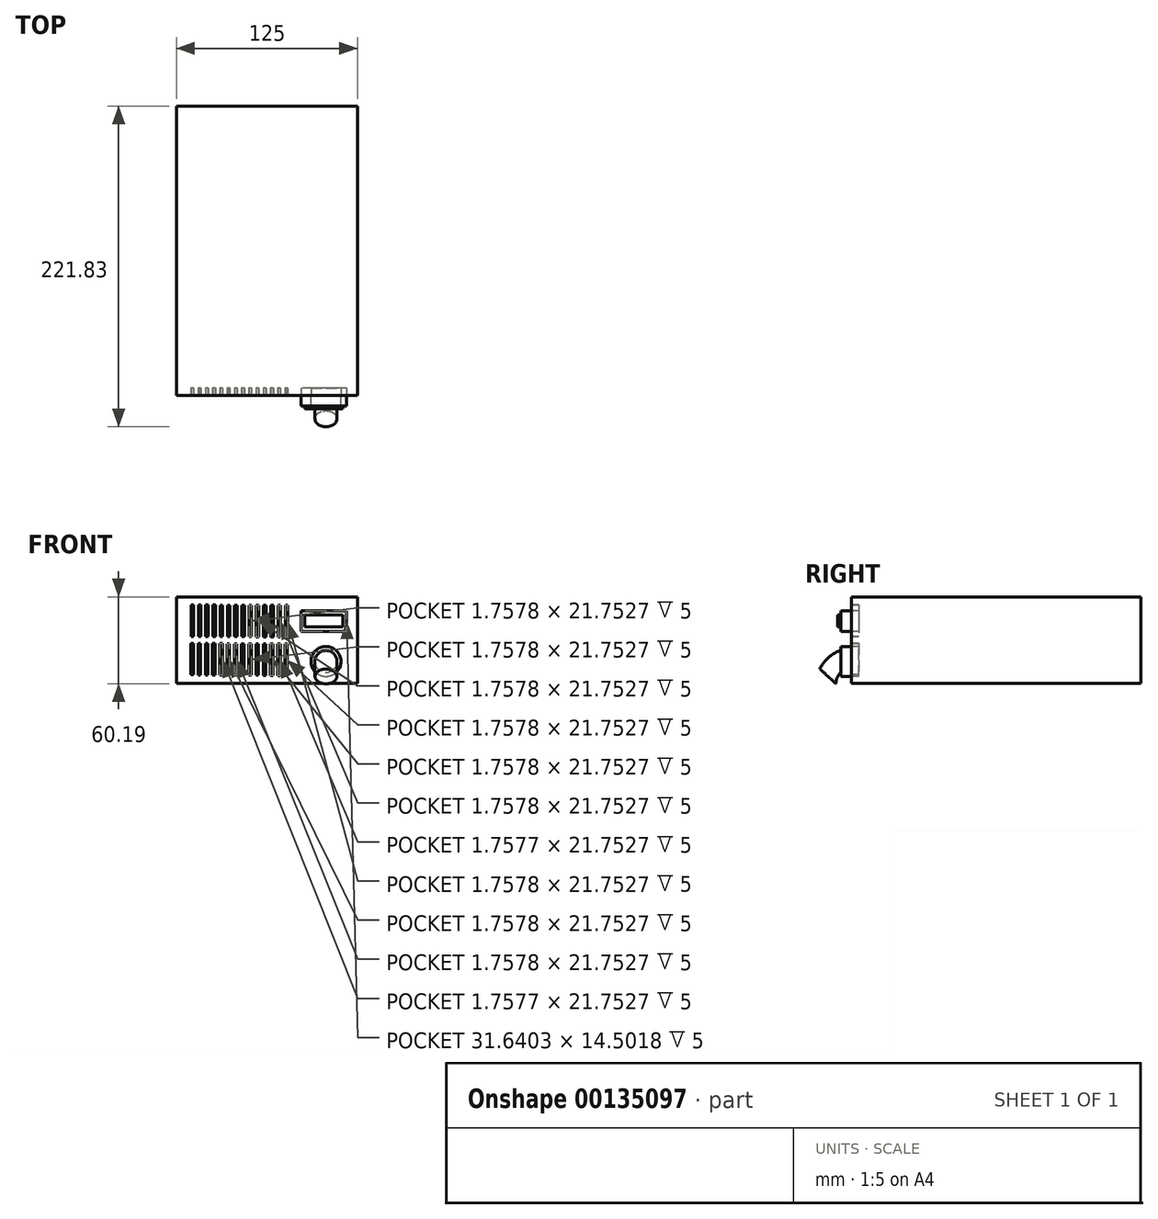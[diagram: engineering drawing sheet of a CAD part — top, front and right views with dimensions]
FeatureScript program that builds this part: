
annotation { "Feature Type Name" : "Feature", "Feature Type Description" : "" }
export const myFeature = defineFeature(function(context is Context, id is Id, definition is map)
    precondition{}
    {
        {
            var Q0;
            Q0=qCreatedBy(makeId("Front.planeOp"),FACE);
            var sketch = newSketch(context, id + "F0", { "sketchPlane" : qUnion([Q0])});
            skLineSegment(sketch, "E0.bottom", {"start": v(-38.13, -24.78) * mm, "end": v(86.87, -24.78) * mm});
            skLineSegment(sketch, "E0.top", {"start": v(-38.13, 35.22) * mm, "end": v(86.87, 35.22) * mm});
            skLineSegment(sketch, "E0.left", {"start": v(-38.13, -24.78) * mm, "end": v(-38.13, 35.22) * mm});
            skLineSegment(sketch, "E0.right", {"start": v(86.87, -24.78) * mm, "end": v(86.87, 35.22) * mm});
            skSolve(sketch);
        }
        {
            var Q0;
            Q0=makeQuery(id+"F0.imprint","IMPRINT",FACE,{"disambiguationData":[TD([[makeQuery(id+"F0.imprint","IMPRINT",EDGE,{"derivedFrom":sQuery(id+"F0.wireOp",EDGE,"E0.bottom")}),1.0]])]});
            extrude(context, id + "F1", {"entities" : qUnion([Q0]), "oppositeDirection" : true, "depth" : 200 * mm});
        }
        {
            var Q0;
            Q0=makeQuery(id+"F1.opExtrude","CAP_FACE",FACE,{"disambiguationData":[OSD([sQuery(id+"F0.wireOp",EDGE,"E0.bottom"),sQuery(id+"F0.wireOp",EDGE,"E0.top"),sQuery(id+"F0.wireOp",EDGE,"E0.left"),sQuery(id+"F0.wireOp",EDGE,"E0.right")])],"isStart":true});
            var sketch = newSketch(context, id + "F2", { "sketchPlane" : qUnion([Q0])});
            skLineSegment(sketch, "E1.bottom", {"start": v(79.42, 25.68) * mm, "end": v(47.78, 25.68) * mm});
            skLineSegment(sketch, "E1.top", {"start": v(79.42, 11.18) * mm, "end": v(47.78, 11.18) * mm});
            skLineSegment(sketch, "E1.left", {"start": v(79.42, 25.68) * mm, "end": v(79.42, 11.18) * mm});
            skLineSegment(sketch, "E1.right", {"start": v(47.78, 25.68) * mm, "end": v(47.78, 11.18) * mm});
            skCircle(sketch, "E2", {"center": v(65.14, -9.48) * mm, "radius": 10.36 * mm});
            skLineSegment(sketch, "E3.bottom", {"start": v(-26.27, 29.64) * mm, "end": v(-28.03, 29.64) * mm});
            skLineSegment(sketch, "E3.top", {"start": v(-26.27, 7.88) * mm, "end": v(-28.03, 7.88) * mm});
            skLineSegment(sketch, "E3.left", {"start": v(-26.27, 29.64) * mm, "end": v(-26.27, 7.88) * mm});
            skLineSegment(sketch, "E3.right", {"start": v(-28.03, 29.64) * mm, "end": v(-28.03, 7.88) * mm});
            skLineSegment(sketch, "E4.0.1.0", {"start": v(-28.25, 3) * mm, "end": v(-28.25, -18.75) * mm});
            skLineSegment(sketch, "E4.0.1.1", {"start": v(-26.49, 3) * mm, "end": v(-26.49, -18.75) * mm});
            skLineSegment(sketch, "E4.0.1.2", {"start": v(-26.49, 3) * mm, "end": v(-28.25, 3) * mm});
            skLineSegment(sketch, "E4.0.1.3", {"start": v(-26.49, -18.75) * mm, "end": v(-28.25, -18.75) * mm});
            skLineSegment(sketch, "E4.1.0.0", {"start": v(-23.03, 29.6) * mm, "end": v(-23.03, 7.85) * mm});
            skLineSegment(sketch, "E4.1.0.1", {"start": v(-21.27, 29.6) * mm, "end": v(-21.27, 7.85) * mm});
            skLineSegment(sketch, "E4.1.0.2", {"start": v(-21.27, 29.6) * mm, "end": v(-23.03, 29.6) * mm});
            skLineSegment(sketch, "E4.1.0.3", {"start": v(-21.27, 7.85) * mm, "end": v(-23.03, 7.85) * mm});
            skLineSegment(sketch, "E4.1.1.0", {"start": v(-23.25, 2.97) * mm, "end": v(-23.25, -18.79) * mm});
            skLineSegment(sketch, "E4.1.1.1", {"start": v(-21.49, 2.97) * mm, "end": v(-21.49, -18.79) * mm});
            skLineSegment(sketch, "E4.1.1.2", {"start": v(-21.49, 2.97) * mm, "end": v(-23.25, 2.97) * mm});
            skLineSegment(sketch, "E4.1.1.3", {"start": v(-21.49, -18.79) * mm, "end": v(-23.25, -18.79) * mm});
            skLineSegment(sketch, "E4.2.0.0", {"start": v(-18.03, 29.57) * mm, "end": v(-18.03, 7.82) * mm});
            skLineSegment(sketch, "E4.2.0.1", {"start": v(-16.27, 29.57) * mm, "end": v(-16.27, 7.82) * mm});
            skLineSegment(sketch, "E4.2.0.2", {"start": v(-16.27, 29.57) * mm, "end": v(-18.03, 29.57) * mm});
            skLineSegment(sketch, "E4.2.0.3", {"start": v(-16.27, 7.82) * mm, "end": v(-18.03, 7.82) * mm});
            skLineSegment(sketch, "E4.2.1.0", {"start": v(-18.25, 2.93) * mm, "end": v(-18.25, -18.82) * mm});
            skLineSegment(sketch, "E4.2.1.1", {"start": v(-16.49, 2.93) * mm, "end": v(-16.49, -18.82) * mm});
            skLineSegment(sketch, "E4.2.1.2", {"start": v(-16.49, 2.93) * mm, "end": v(-18.25, 2.93) * mm});
            skLineSegment(sketch, "E4.2.1.3", {"start": v(-16.49, -18.82) * mm, "end": v(-18.25, -18.82) * mm});
            skLineSegment(sketch, "E4.direction1", {"start": v(-28.03, 7.88) * mm, "end": v(-23.03, 7.85) * mm, "construction": true});
            skLineSegment(sketch, "E4.direction2", {"start": v(-28.03, 7.88) * mm, "end": v(-28.25, -18.75) * mm, "construction": true});
            skLineSegment(sketch, "E5.0.3.0", {"start": v(-13.03, 29.53) * mm, "end": v(-13.03, 7.78) * mm});
            skLineSegment(sketch, "E5.3.3.0", {"start": v(-11.27, 29.53) * mm, "end": v(-11.27, 7.78) * mm});
            skLineSegment(sketch, "E5.6.3.0", {"start": v(-11.27, 29.53) * mm, "end": v(-13.03, 29.53) * mm});
            skLineSegment(sketch, "E5.9.3.0", {"start": v(-11.27, 7.78) * mm, "end": v(-13.03, 7.78) * mm});
            skLineSegment(sketch, "E5.0.3.1", {"start": v(-13.25, 2.9) * mm, "end": v(-13.25, -18.85) * mm});
            skLineSegment(sketch, "E5.3.3.1", {"start": v(-11.49, 2.9) * mm, "end": v(-11.49, -18.85) * mm});
            skLineSegment(sketch, "E5.6.3.1", {"start": v(-11.49, 2.9) * mm, "end": v(-13.25, 2.9) * mm});
            skLineSegment(sketch, "E5.9.3.1", {"start": v(-11.49, -18.85) * mm, "end": v(-13.25, -18.85) * mm});
            skLineSegment(sketch, "E5.0.4.0", {"start": v(-8.03, 29.5) * mm, "end": v(-8.03, 7.75) * mm});
            skLineSegment(sketch, "E5.3.4.0", {"start": v(-6.27, 29.5) * mm, "end": v(-6.27, 7.75) * mm});
            skLineSegment(sketch, "E5.6.4.0", {"start": v(-6.27, 29.5) * mm, "end": v(-8.03, 29.5) * mm});
            skLineSegment(sketch, "E5.9.4.0", {"start": v(-6.27, 7.75) * mm, "end": v(-8.03, 7.75) * mm});
            skLineSegment(sketch, "E5.0.4.1", {"start": v(-8.25, 2.87) * mm, "end": v(-8.25, -18.89) * mm});
            skLineSegment(sketch, "E5.3.4.1", {"start": v(-6.49, 2.87) * mm, "end": v(-6.49, -18.89) * mm});
            skLineSegment(sketch, "E5.6.4.1", {"start": v(-6.49, 2.87) * mm, "end": v(-8.25, 2.87) * mm});
            skLineSegment(sketch, "E5.9.4.1", {"start": v(-6.49, -18.89) * mm, "end": v(-8.25, -18.89) * mm});
            skLineSegment(sketch, "E5.0.5.0", {"start": v(-3.03, 29.47) * mm, "end": v(-3.03, 7.72) * mm});
            skLineSegment(sketch, "E5.3.5.0", {"start": v(-1.27, 29.47) * mm, "end": v(-1.27, 7.72) * mm});
            skLineSegment(sketch, "E5.6.5.0", {"start": v(-1.27, 29.47) * mm, "end": v(-3.03, 29.47) * mm});
            skLineSegment(sketch, "E5.9.5.0", {"start": v(-1.27, 7.72) * mm, "end": v(-3.03, 7.72) * mm});
            skLineSegment(sketch, "E5.0.5.1", {"start": v(-3.25, 2.83) * mm, "end": v(-3.25, -18.92) * mm});
            skLineSegment(sketch, "E5.3.5.1", {"start": v(-1.49, 2.83) * mm, "end": v(-1.49, -18.92) * mm});
            skLineSegment(sketch, "E5.6.5.1", {"start": v(-1.49, 2.83) * mm, "end": v(-3.25, 2.83) * mm});
            skLineSegment(sketch, "E5.9.5.1", {"start": v(-1.49, -18.92) * mm, "end": v(-3.25, -18.92) * mm});
            skLineSegment(sketch, "E5.0.6.0", {"start": v(1.97, 29.43) * mm, "end": v(1.97, 7.68) * mm});
            skLineSegment(sketch, "E5.3.6.0", {"start": v(3.73, 29.43) * mm, "end": v(3.73, 7.68) * mm});
            skLineSegment(sketch, "E5.6.6.0", {"start": v(3.73, 29.43) * mm, "end": v(1.97, 29.43) * mm});
            skLineSegment(sketch, "E5.9.6.0", {"start": v(3.73, 7.68) * mm, "end": v(1.97, 7.68) * mm});
            skLineSegment(sketch, "E5.0.6.1", {"start": v(1.75, 2.8) * mm, "end": v(1.75, -18.95) * mm});
            skLineSegment(sketch, "E5.3.6.1", {"start": v(3.51, 2.8) * mm, "end": v(3.51, -18.95) * mm});
            skLineSegment(sketch, "E5.6.6.1", {"start": v(3.51, 2.8) * mm, "end": v(1.75, 2.8) * mm});
            skLineSegment(sketch, "E5.9.6.1", {"start": v(3.51, -18.95) * mm, "end": v(1.75, -18.95) * mm});
            skLineSegment(sketch, "E5.0.7.0", {"start": v(6.97, 29.4) * mm, "end": v(6.97, 7.65) * mm});
            skLineSegment(sketch, "E5.3.7.0", {"start": v(8.73, 29.4) * mm, "end": v(8.73, 7.65) * mm});
            skLineSegment(sketch, "E5.6.7.0", {"start": v(8.73, 29.4) * mm, "end": v(6.97, 29.4) * mm});
            skLineSegment(sketch, "E5.9.7.0", {"start": v(8.73, 7.65) * mm, "end": v(6.97, 7.65) * mm});
            skLineSegment(sketch, "E5.0.7.1", {"start": v(6.75, 2.77) * mm, "end": v(6.75, -18.99) * mm});
            skLineSegment(sketch, "E5.3.7.1", {"start": v(8.51, 2.77) * mm, "end": v(8.51, -18.99) * mm});
            skLineSegment(sketch, "E5.6.7.1", {"start": v(8.51, 2.77) * mm, "end": v(6.75, 2.77) * mm});
            skLineSegment(sketch, "E5.9.7.1", {"start": v(8.51, -18.99) * mm, "end": v(6.75, -18.99) * mm});
            skLineSegment(sketch, "E5.0.8.0", {"start": v(11.97, 29.37) * mm, "end": v(11.97, 7.61) * mm});
            skLineSegment(sketch, "E5.3.8.0", {"start": v(13.73, 29.37) * mm, "end": v(13.73, 7.61) * mm});
            skLineSegment(sketch, "E5.6.8.0", {"start": v(13.73, 29.37) * mm, "end": v(11.97, 29.37) * mm});
            skLineSegment(sketch, "E5.9.8.0", {"start": v(13.73, 7.61) * mm, "end": v(11.97, 7.61) * mm});
            skLineSegment(sketch, "E5.0.8.1", {"start": v(11.75, 2.73) * mm, "end": v(11.75, -19.02) * mm});
            skLineSegment(sketch, "E5.3.8.1", {"start": v(13.51, 2.73) * mm, "end": v(13.51, -19.02) * mm});
            skLineSegment(sketch, "E5.6.8.1", {"start": v(13.51, 2.73) * mm, "end": v(11.75, 2.73) * mm});
            skLineSegment(sketch, "E5.9.8.1", {"start": v(13.51, -19.02) * mm, "end": v(11.75, -19.02) * mm});
            skLineSegment(sketch, "E5.0.9.0", {"start": v(16.97, 29.33) * mm, "end": v(16.97, 7.58) * mm});
            skLineSegment(sketch, "E5.3.9.0", {"start": v(18.73, 29.33) * mm, "end": v(18.73, 7.58) * mm});
            skLineSegment(sketch, "E5.6.9.0", {"start": v(18.73, 29.33) * mm, "end": v(16.97, 29.33) * mm});
            skLineSegment(sketch, "E5.9.9.0", {"start": v(18.73, 7.58) * mm, "end": v(16.97, 7.58) * mm});
            skLineSegment(sketch, "E5.0.9.1", {"start": v(16.75, 2.7) * mm, "end": v(16.75, -19.05) * mm});
            skLineSegment(sketch, "E5.3.9.1", {"start": v(18.51, 2.7) * mm, "end": v(18.51, -19.05) * mm});
            skLineSegment(sketch, "E5.6.9.1", {"start": v(18.51, 2.7) * mm, "end": v(16.75, 2.7) * mm});
            skLineSegment(sketch, "E5.9.9.1", {"start": v(18.51, -19.05) * mm, "end": v(16.75, -19.05) * mm});
            skLineSegment(sketch, "E5.0.10.0", {"start": v(21.97, 29.3) * mm, "end": v(21.97, 7.55) * mm});
            skLineSegment(sketch, "E5.3.10.0", {"start": v(23.73, 29.3) * mm, "end": v(23.73, 7.55) * mm});
            skLineSegment(sketch, "E5.6.10.0", {"start": v(23.73, 29.3) * mm, "end": v(21.97, 29.3) * mm});
            skLineSegment(sketch, "E5.9.10.0", {"start": v(23.73, 7.55) * mm, "end": v(21.97, 7.55) * mm});
            skLineSegment(sketch, "E5.0.10.1", {"start": v(21.75, 2.66) * mm, "end": v(21.75, -19.09) * mm});
            skLineSegment(sketch, "E5.3.10.1", {"start": v(23.51, 2.66) * mm, "end": v(23.51, -19.09) * mm});
            skLineSegment(sketch, "E5.6.10.1", {"start": v(23.51, 2.66) * mm, "end": v(21.75, 2.66) * mm});
            skLineSegment(sketch, "E5.9.10.1", {"start": v(23.51, -19.09) * mm, "end": v(21.75, -19.09) * mm});
            skLineSegment(sketch, "E5.0.11.0", {"start": v(26.97, 29.27) * mm, "end": v(26.97, 7.51) * mm});
            skLineSegment(sketch, "E5.3.11.0", {"start": v(28.73, 29.27) * mm, "end": v(28.73, 7.51) * mm});
            skLineSegment(sketch, "E5.6.11.0", {"start": v(28.73, 29.27) * mm, "end": v(26.97, 29.27) * mm});
            skLineSegment(sketch, "E5.9.11.0", {"start": v(28.73, 7.51) * mm, "end": v(26.97, 7.51) * mm});
            skLineSegment(sketch, "E5.0.11.1", {"start": v(26.75, 2.63) * mm, "end": v(26.75, -19.12) * mm});
            skLineSegment(sketch, "E5.3.11.1", {"start": v(28.51, 2.63) * mm, "end": v(28.51, -19.12) * mm});
            skLineSegment(sketch, "E5.6.11.1", {"start": v(28.51, 2.63) * mm, "end": v(26.75, 2.63) * mm});
            skLineSegment(sketch, "E5.9.11.1", {"start": v(28.51, -19.12) * mm, "end": v(26.75, -19.12) * mm});
            skLineSegment(sketch, "E5.0.12.0", {"start": v(31.97, 29.23) * mm, "end": v(31.97, 7.48) * mm});
            skLineSegment(sketch, "E5.3.12.0", {"start": v(33.73, 29.23) * mm, "end": v(33.73, 7.48) * mm});
            skLineSegment(sketch, "E5.6.12.0", {"start": v(33.73, 29.23) * mm, "end": v(31.97, 29.23) * mm});
            skLineSegment(sketch, "E5.9.12.0", {"start": v(33.73, 7.48) * mm, "end": v(31.97, 7.48) * mm});
            skLineSegment(sketch, "E5.0.12.1", {"start": v(31.75, 2.6) * mm, "end": v(31.75, -19.16) * mm});
            skLineSegment(sketch, "E5.3.12.1", {"start": v(33.51, 2.6) * mm, "end": v(33.51, -19.16) * mm});
            skLineSegment(sketch, "E5.6.12.1", {"start": v(33.51, 2.6) * mm, "end": v(31.75, 2.6) * mm});
            skLineSegment(sketch, "E5.9.12.1", {"start": v(33.51, -19.16) * mm, "end": v(31.75, -19.16) * mm});
            skLineSegment(sketch, "E5.0.13.0", {"start": v(36.97, 29.2) * mm, "end": v(36.97, 7.45) * mm});
            skLineSegment(sketch, "E5.3.13.0", {"start": v(38.73, 29.2) * mm, "end": v(38.73, 7.45) * mm});
            skLineSegment(sketch, "E5.6.13.0", {"start": v(38.73, 29.2) * mm, "end": v(36.97, 29.2) * mm});
            skLineSegment(sketch, "E5.9.13.0", {"start": v(38.73, 7.45) * mm, "end": v(36.97, 7.45) * mm});
            skLineSegment(sketch, "E5.0.13.1", {"start": v(36.75, 2.56) * mm, "end": v(36.75, -19.19) * mm});
            skLineSegment(sketch, "E5.3.13.1", {"start": v(38.51, 2.56) * mm, "end": v(38.51, -19.19) * mm});
            skLineSegment(sketch, "E5.6.13.1", {"start": v(38.51, 2.56) * mm, "end": v(36.75, 2.56) * mm});
            skLineSegment(sketch, "E5.9.13.1", {"start": v(38.51, -19.19) * mm, "end": v(36.75, -19.19) * mm});
            skSolve(sketch);
        }
        {
            var Q0;
            Q0=makeQuery(id+"F2.imprint","IMPRINT",FACE,{"disambiguationData":[TD([[makeQuery(id+"F2.imprint","IMPRINT",EDGE,{"derivedFrom":sQuery(id+"F2.wireOp",EDGE,"E1.bottom")}),1.0]])]});
            var Q1;
            Q1=makeQuery(id+"F2.imprint","IMPRINT",FACE,{"disambiguationData":[TD([[makeQuery(id+"F2.imprint","IMPRINT",EDGE,{"derivedFrom":sQuery(id+"F2.wireOp",EDGE,"E2")}),1.0]])]});
            extrude(context, id + "F3", {"entities" : qUnion([Q0, Q1]), "operationType" : NewBodyOperationType.ADD, "depth" : 7.4 * mm});
        }
        {
            var Q0;
            Q0 = qSketchRegion(id + "F2", true);
            extrude(context, id + "F4", {"entities" : qUnion([Q0]), "operationType" : NewBodyOperationType.REMOVE, "oppositeDirection" : true, "depth" : 5 * mm});
        }
        {
            var Q0;
            Q0=makeQuery(id+"F3.opExtrude","CAP_FACE",FACE,{"disambiguationData":[OSD([sQuery(id+"F2.wireOp",EDGE,"E1.bottom"),sQuery(id+"F2.wireOp",EDGE,"E1.top"),sQuery(id+"F2.wireOp",EDGE,"E1.left"),sQuery(id+"F2.wireOp",EDGE,"E1.right")])],"isStart":false});
            var sketch = newSketch(context, id + "F5", { "sketchPlane" : qUnion([Q0])});
            skLineSegment(sketch, "E6.bottom", {"start": v(50.6, 22.76) * mm, "end": v(76.73, 22.76) * mm});
            skLineSegment(sketch, "E6.top", {"start": v(50.6, 14.27) * mm, "end": v(76.73, 14.27) * mm});
            skLineSegment(sketch, "E6.left", {"start": v(50.6, 22.76) * mm, "end": v(50.6, 14.27) * mm});
            skLineSegment(sketch, "E6.right", {"start": v(76.73, 22.76) * mm, "end": v(76.73, 14.27) * mm});
            skSolve(sketch);
        }
        {
            var Q0;
            Q0=makeQuery(id+"F5.imprint","IMPRINT",FACE,{"disambiguationData":[TD([[makeQuery(id+"F5.imprint","IMPRINT",EDGE,{"derivedFrom":sQuery(id+"F5.wireOp",EDGE,"E6.bottom")}),-1.0]])]});
            extrude(context, id + "F6", {"entities" : qUnion([Q0]), "operationType" : NewBodyOperationType.ADD, "depth" : 2 * mm});
        }
        {
            var Q0;
            Q0=makeQuery(id+"F3.opExtrude","CAP_FACE",FACE,{"disambiguationData":[OSD([sQuery(id+"F2.wireOp",EDGE,"E2")])],"isStart":false});
            var sketch = newSketch(context, id + "F7", { "sketchPlane" : qUnion([Q0])});
            skCircle(sketch, "E7", {"center": v(65.14, -9.48) * mm, "radius": 7.58 * mm});
            skSolve(sketch);
        }
        {
            var Q0;
            Q0=makeQuery(id+"F7.imprint","IMPRINT",FACE,{"disambiguationData":[TD([[makeQuery(id+"F7.imprint","IMPRINT",EDGE,{"derivedFrom":sQuery(id+"F7.wireOp",EDGE,"E7")}),1.0]])]});
            var Q1;
            Q1=makeQuery(id+"F1.opExtrude","CAP_EDGE",EDGE,{"disambiguationData":[OSD([sQuery(id+"F0.wireOp",EDGE,"E0.bottom")])],"isStart":true});
            revolve(context, id + "F8", {"operationType" : NewBodyOperationType.ADD, "entities" : qUnion([Q0]), "axis" : qUnion([Q1]), "revolveType" : RevolveType.ONE_DIRECTION, "angle" : 47.24 * degree});
        }
    });
